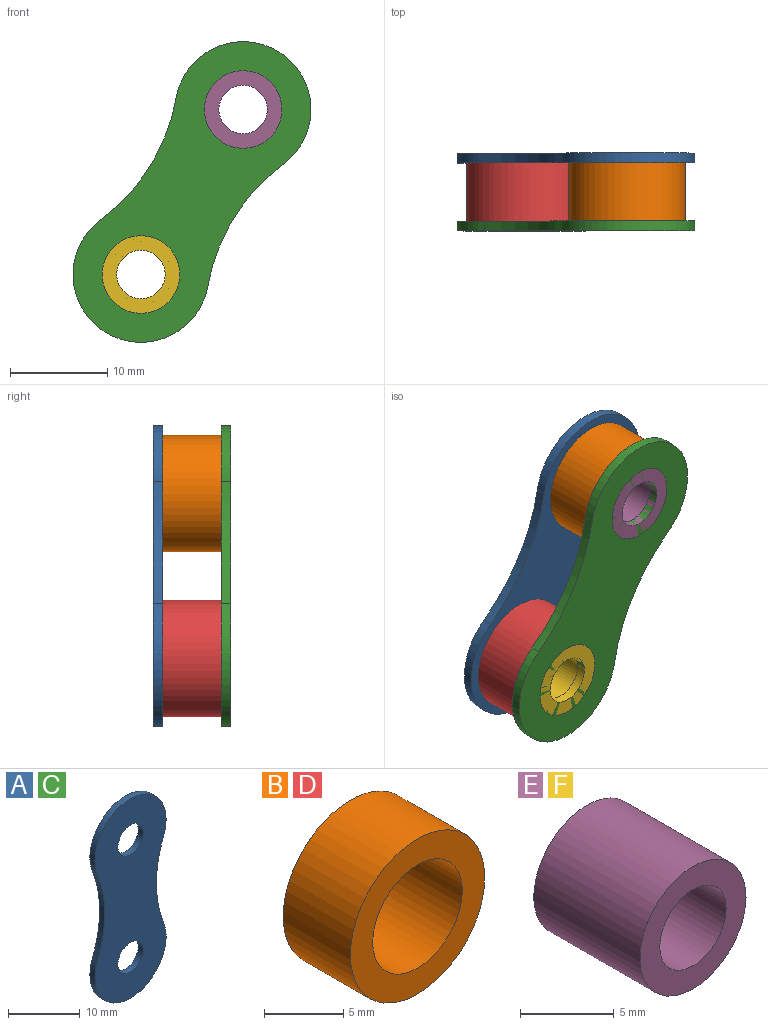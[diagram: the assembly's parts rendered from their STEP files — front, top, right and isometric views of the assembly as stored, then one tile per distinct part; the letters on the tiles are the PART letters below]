
ASSEMBLY  parts=6 mates=6
PART A: 8 faces, bbox 14x1x34 mm
  f0: cylinder r=20mm len=14.82mm, axis (0,1,0), area 15.2mm2, adj f1,f5,f6,f7
  f1: cylinder r=7mm len=14mm, axis (0,1,0), area 27.3mm2, adj f0,f2,f6,f7
  f2: cylinder r=20mm len=14.82mm, axis (0,1,0), area 15.2mm2, adj f1,f5,f6,f7
  f3: cylinder r=2.5mm len=5mm, axis (0,1,0), area 15.7mm2, adj f6,f7
  f4: cylinder r=2.5mm len=5mm, axis (0,1,0), area 15.7mm2, adj f6,f7
  f5: cylinder r=7mm len=14mm, axis (0,1,0), area 27.3mm2, adj f0,f2,f6,f7
  f6: plane 34x14mm, normal (0,-1,0), area 349.9mm2, adj f0,f1,f2,f3,f4,f5
  f7: plane 34x14mm, normal (0,1,0), area 349.9mm2, adj f0,f1,f2,f3,f4,f5
PART B: 4 faces, bbox 12x6x12 mm
  f0: cylinder r=4mm len=8mm, axis (0,1,0), area 150.8mm2, adj f2,f3
  f1: cylinder r=6mm len=12mm, axis (0,1,0), area 226.2mm2, adj f2,f3
  f2: plane 12x12mm, normal (0,-1,0), area 62.8mm2, adj f0,f1
  f3: plane 12x12mm, normal (0,1,0), area 62.8mm2, adj f0,f1
PART C: same geometry as A
PART D: same geometry as B
PART E: 4 faces, bbox 8x8x8 mm
  f0: cylinder r=2.5mm len=8mm, axis (0,1,0), area 125.7mm2, adj f2,f3
  f1: cylinder r=4mm len=8mm, axis (0,1,0), area 201.1mm2, adj f2,f3
  f2: plane 8x8mm, normal (0,-1,0), area 30.6mm2, adj f0,f1
  f3: plane 8x8mm, normal (0,1,0), area 30.6mm2, adj f0,f1
PART F: same geometry as E
PLACE A rot(axis=(0,1,0),31.8deg) t=(42.85,19.27,4.99)mm
PLACE B rot(axis=(0,1,0),31.8deg) t=(42.85,18.27,4.99)mm
PLACE C rot(axis=(0,1,0),31.8deg) t=(42.85,12.27,4.99)mm
PLACE D rot(axis=(0,-1,0),1.5deg) t=(32.32,18.27,-12.01)mm
PLACE E rot(axis=(0,1,0),31.8deg) t=(42.85,19.27,4.99)mm
PLACE F rot(axis=(0,1,0),31.8deg) t=(32.32,19.27,-12.01)mm
MATE fastened F.f0 <-> C.f1  axis (0,-1,0) through (32.32,11.27,-12.01)mm
MATE fastened F.f0 <-> A.f1  axis (0,1,0) through (32.32,19.27,-12.01)mm
MATE revolute B.f0 <-> C.f3  axis (0,-1,0) through (42.85,12.27,4.99)mm
MATE revolute D.f0 <-> A.f1  axis (0,1,0) through (32.32,18.27,-12.01)mm
MATE fastened E.f0 <-> C.f3  axis (0,-1,0) through (42.85,11.27,4.99)mm
MATE fastened F.f0 <-> C.f1  axis (0,-1,0) through (32.32,11.27,-12.01)mm
